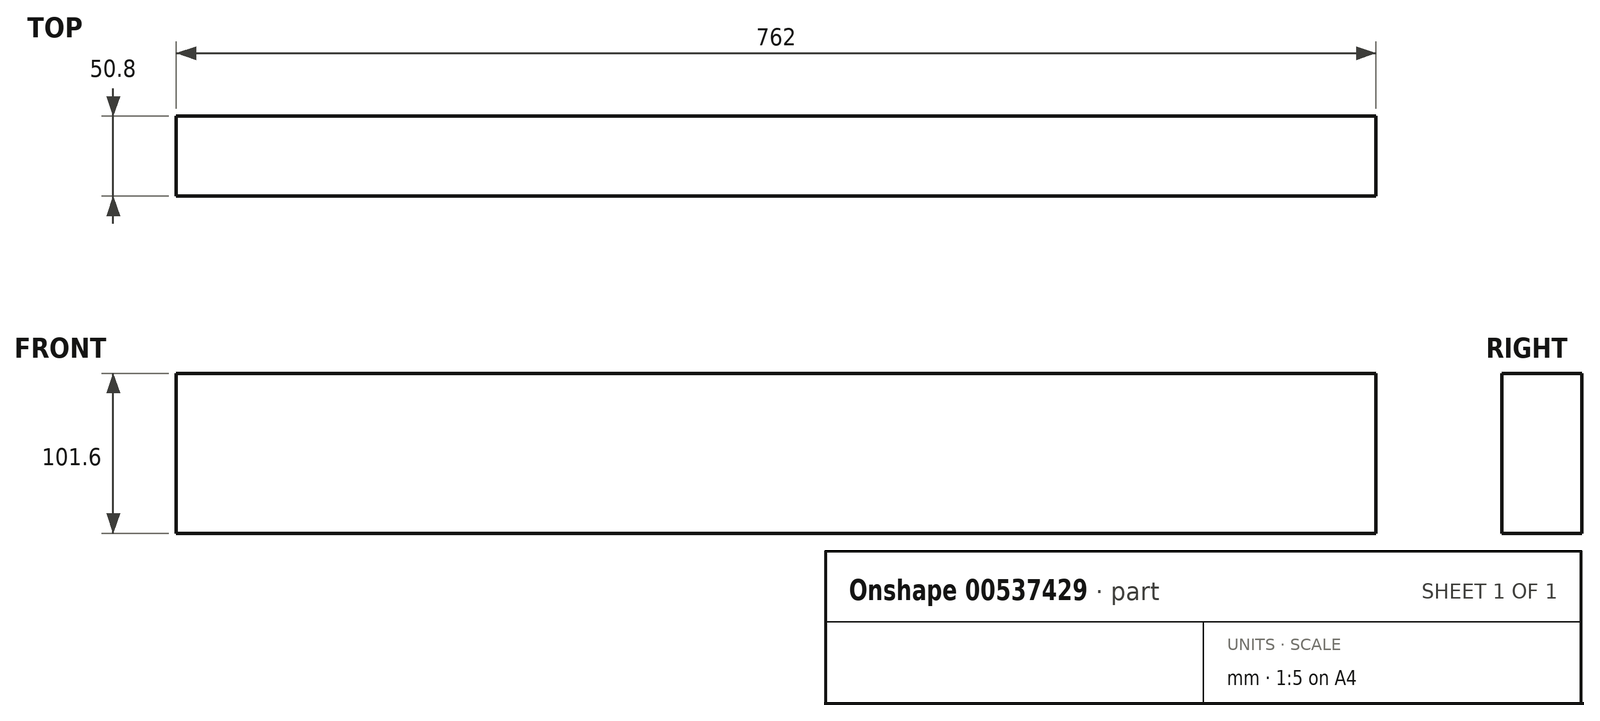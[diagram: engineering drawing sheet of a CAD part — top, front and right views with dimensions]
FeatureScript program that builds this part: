
annotation { "Feature Type Name" : "Feature", "Feature Type Description" : "" }
export const myFeature = defineFeature(function(context is Context, id is Id, definition is map)
    precondition{}
    {
        {
            var Q0;
            Q0=qCreatedBy(makeId("Front.planeOp"),FACE);
            var sketch = newSketch(context, id + "F0", { "sketchPlane" : qUnion([Q0])});
            skLineSegment(sketch, "E0.bottom", {"start": v(381, 50.8) * mm, "end": v(-381, 50.8) * mm});
            skLineSegment(sketch, "E0.top", {"start": v(381, -50.8) * mm, "end": v(-381, -50.8) * mm});
            skLineSegment(sketch, "E0.left", {"start": v(381, 50.8) * mm, "end": v(381, -50.8) * mm});
            skLineSegment(sketch, "E0.right", {"start": v(-381, 50.8) * mm, "end": v(-381, -50.8) * mm});
            skPoint(sketch, "E0.middle", {"position": v(0, 0) * mm});
            skSolve(sketch);
        }
        {
            var Q0;
            Q0 = qSketchRegion(id + "F0", true);
            extrude(context, id + "F1", {"entities" : qUnion([Q0]), "depth" : 50.8 * mm, "offsetDistance" : 25.4 * mm});
        }
    });
